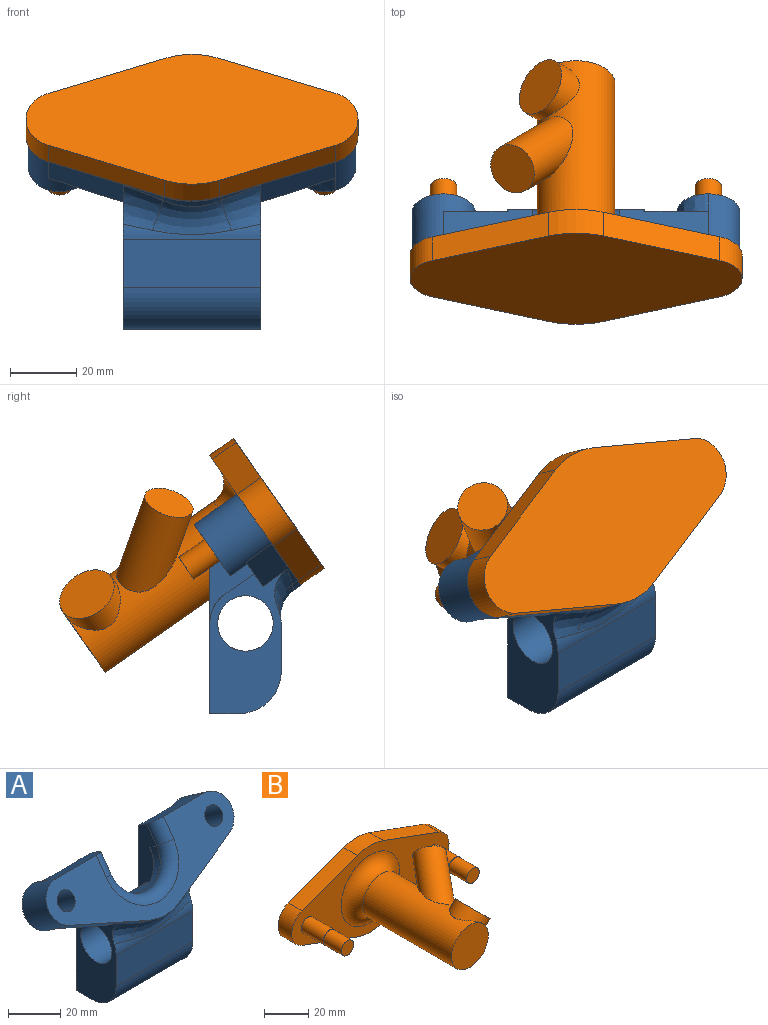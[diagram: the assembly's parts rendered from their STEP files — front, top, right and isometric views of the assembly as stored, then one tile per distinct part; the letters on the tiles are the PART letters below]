
ASSEMBLY  parts=2 mates=1
PART A: 44 faces, bbox 100.3x33.5x67.5 mm
  f0: cylinder r=10.79mm len=41.66mm, axis (-1,0,0), area 293.2mm2, adj f3,f4,f5,f8,f14,f16,f22,f23
  f1: plane 22.97x22.34mm, normal (0,0.82,-0.57), area 316.5mm2, adj f10,f17,f22,f23,f25,f37
  f2: plane 26.86x8.32mm, normal (0,0.57,0.82), area 255mm2, adj f4,f9,f13,f14,f27,f29,f30
  f3: plane 7.37x0.17mm, normal (0,0.82,-0.57), area 1.5mm2, adj f0,f16,f25,f28
  f4: plane 32.64x13.52mm, normal (-1,0,0), area 199.4mm2, adj f0,f2,f5,f9,f26,f29
  f5: plane 8.84x6.19mm, normal (0,0.57,0.82), area 3.4mm2, adj f0,f4,f9,f24
  f6: plane 13.14x10.77mm, normal (0,0.82,-0.57), area 37.1mm2, adj f8,f14,f15
  f7: cylinder r=10.79mm len=41.66mm, axis (-1,0,0), area 111.2mm2, adj f23,f24,f34,f35,f36,f40
  f8: plane 26.29x8.84mm, normal (0,0.57,0.82), area 283.8mm2, adj f0,f6,f14,f16,f21
  f9: plane 22.97x22.34mm, normal (0,0.82,-0.57), area 316.5mm2, adj f2,f4,f5,f12,f13,f24
  f10: plane 34.77x15.69mm, normal (0.37,-0.53,-0.76), area 247.2mm2, adj f1,f11,f20,f23,f27,f34
  f11: cylinder r=24.13mm len=17.62mm, axis (0,-0.82,0.57), area 45mm2, adj f10,f12,f27,f35
  f12: plane 34.77x15.69mm, normal (-0.37,-0.53,-0.76), area 247.2mm2, adj f9,f11,f13,f24,f27,f36
  f13: cylinder r=9.53mm len=24.71mm, axis (0,-0.82,0.57), area 631.1mm2, adj f2,f9,f12,f27,f39
  f14: plane 35.19x13.52mm, normal (1,0,0), area 241.7mm2, adj f0,f2,f6,f8,f15,f26,f29,f30
  f15: cylinder r=13.14mm len=26.29mm, axis (0,-0.82,0.57), area 183.6mm2, adj f6,f14,f16,f21,f31
  f16: plane 35.19x13.52mm, normal (-1,0,0), area 241.7mm2, adj f0,f3,f8,f15,f17,f21,f28,f32
  f17: plane 26.86x8.32mm, normal (0,0.57,0.82), area 255mm2, adj f1,f16,f20,f25,f27,f28,f32
  f18: cylinder r=4.25mm len=17.88mm, axis (0,-0.82,0.57), area 423.9mm2, adj f27,f39
  f19: cylinder r=4.25mm len=17.88mm, axis (0,-0.82,0.57), area 423.9mm2, adj f27,f38
  f20: cylinder r=9.53mm len=24.17mm, axis (0,-0.82,0.57), area 418.5mm2, adj f10,f17,f27,f37,f38
  f21: plane 13.14x10.77mm, normal (0,0.82,-0.57), area 37.1mm2, adj f8,f15,f16
  f22: plane 8.84x6.19mm, normal (0,0.57,0.82), area 3.4mm2, adj f0,f1,f23,f25
  f23: plane 44.74x24.49mm, normal (1,0,0), area 557.4mm2, adj f0,f1,f7,f10,f22,f33,f34,f40
  f24: plane 44.74x24.49mm, normal (-1,0,0), area 557.4mm2, adj f0,f5,f7,f9,f12,f33,f36,f40
  f25: plane 32.64x13.52mm, normal (1,0,0), area 199.4mm2, adj f0,f1,f3,f17,f22,f28
  f26: plane 7.37x0.17mm, normal (0,0.82,-0.57), area 1.5mm2, adj f0,f4,f14,f29
  f27: plane 99.06x27.57mm, normal (0,-0.82,0.57), area 1501.9mm2, adj f2,f10,f11,f12,f13,f17,f18,f19
  f28: plane 32.11x7.37mm, normal (0,1,0), area 236.5mm2, adj f3,f16,f17,f25
  f29: plane 32.11x7.37mm, normal (0,1,0), area 236.5mm2, adj f2,f4,f14,f26
  f30: cylinder r=5.08mm len=10.72mm, axis (0,-0.57,-0.82), area 76mm2, adj f2,f14,f27,f31
  f31: torus R=18.22mm, axis (0,0.82,-0.57), area 375.8mm2, adj f15,f27,f30,f32
  f32: cylinder r=5.08mm len=10.72mm, axis (0,0.57,0.82), area 76mm2, adj f16,f17,f27,f31
  f33: cylinder r=8.38mm len=41.66mm, axis (-1,0,0), area 2193.8mm2, adj f23,f24
  f34: bspline ~27.17x16.98mm, area 129.1mm2, adj f7,f10,f23,f35
  f35: bspline ~28.27x11.25mm, area 210.6mm2, adj f7,f11,f34,f36
  f36: bspline ~27.17x16.98mm, area 129.1mm2, adj f7,f12,f24,f35
  f37: extruded ~19.24x16.12mm, area 212.7mm2, adj f1,f20,f38
  f38: plane 19.06x15.61mm, normal (0,0.82,-0.57), area 228.3mm2, adj f19,f20,f37
  f39: plane 19.05x15.61mm, normal (0,0.82,-0.57), area 228.3mm2, adj f13,f18
  f40: plane 41.66x14.53mm, normal (0,-1,0), area 605.3mm2, adj f7,f23,f24,f43
  f41: plane 41.66x8.89mm, normal (0,0,-1), area 370.3mm2, adj f23,f24,f42,f43
  f42: plane 41.66x27.23mm, normal (0,1,0), area 1134.3mm2, adj f0,f23,f24,f41
  f43: cylinder r=12.7mm len=41.66mm, axis (1,0,0), area 831mm2, adj f23,f24,f40,f41
PART B: 25 faces, bbox 100.3x72.3x51.4 mm
  f0: cylinder r=11.75mm len=56.5mm, axis (0,1,0), area 3615.5mm2, adj f1,f12,f13,f15
  f1: plane 23.5x23.5mm, normal (0,-1,0), area 433.6mm2, adj f0
  f2: plane 35.26x12.94mm, normal (0.34,0,0.94), area 329.1mm2, adj f3,f9,f10,f11
  f3: cylinder r=23.94mm len=16.49mm, axis (0,-1,0), area 147.5mm2, adj f2,f4,f10,f11
  f4: plane 35.26x12.94mm, normal (-0.34,0,0.94), area 329.1mm2, adj f3,f5,f10,f11
  f5: cylinder r=10.16mm len=19.08mm, axis (0,-1,0), area 217.1mm2, adj f4,f6,f10,f11
  f6: plane 35.26x12.94mm, normal (-0.34,0,-0.94), area 329.1mm2, adj f5,f7,f10,f11
  f7: cylinder r=23.94mm len=16.49mm, axis (0,-1,0), area 147.5mm2, adj f6,f8,f10,f11
  f8: plane 35.26x12.94mm, normal (0.34,0,-0.94), area 329.1mm2, adj f7,f9,f10,f11
  f9: cylinder r=10.16mm len=19.08mm, axis (0,-1,0), area 217.1mm2, adj f2,f8,f10,f11
  f10: plane 100.33x47.88mm, normal (0,1,0), area 3216.1mm2, adj f2,f3,f4,f5,f6,f7,f8,f9
  f11: plane 100.33x47.88mm, normal (0,-1,0), area 2004.9mm2, adj f2,f3,f4,f5,f6,f7,f8,f9
  f12: torus R=18.75mm, axis (0,-1,0), area 987.3mm2, adj f0,f11
  f13: cylinder r=9.02mm len=18.2mm, axis (-0.71,0,-0.71), area 310.8mm2, adj f0,f14
  f14: plane 18.03x12.75mm, normal (0.71,0,0.71), area 255.4mm2, adj f13
  f15: cylinder r=7.62mm len=31.54mm, axis (-0.5,-0.71,-0.5), area 1132.7mm2, adj f0,f16
  f16: plane 13.2x13.2mm, normal (0.5,0.71,0.5), area 182.4mm2, adj f15
  f17: cylinder r=4.13mm len=13.97mm, axis (0,1,0), area 362.3mm2, adj f11,f18
  f18: plane 8.26x8.26mm, normal (0,-1,0), area 3.3mm2, adj f17,f20
  f19: plane 8x8mm, normal (0,-1,0), area 50.3mm2, adj f20
  f20: cylinder r=4mm len=11.43mm, axis (0,1,0), area 287.3mm2, adj f18,f19
  f21: cylinder r=4.13mm len=13.97mm, axis (0,1,0), area 362.3mm2, adj f11,f22
  f22: plane 8.26x8.26mm, normal (0,-1,0), area 3.3mm2, adj f21,f24
  f23: plane 8x8mm, normal (0,-1,0), area 50.3mm2, adj f24
  f24: cylinder r=4mm len=11.43mm, axis (0,1,0), area 287.3mm2, adj f22,f23
PLACE A t=(-21.7,-14.63,6.7)mm
PLACE B rot(axis=(0,-0.3,-0.95),180deg) t=(-21.7,-17.23,8.52)mm
MATE cylindrical B.f0 <-> A.f11  axis (0,0.82,-0.57) through (-21.7,-17.23,8.52)mm
